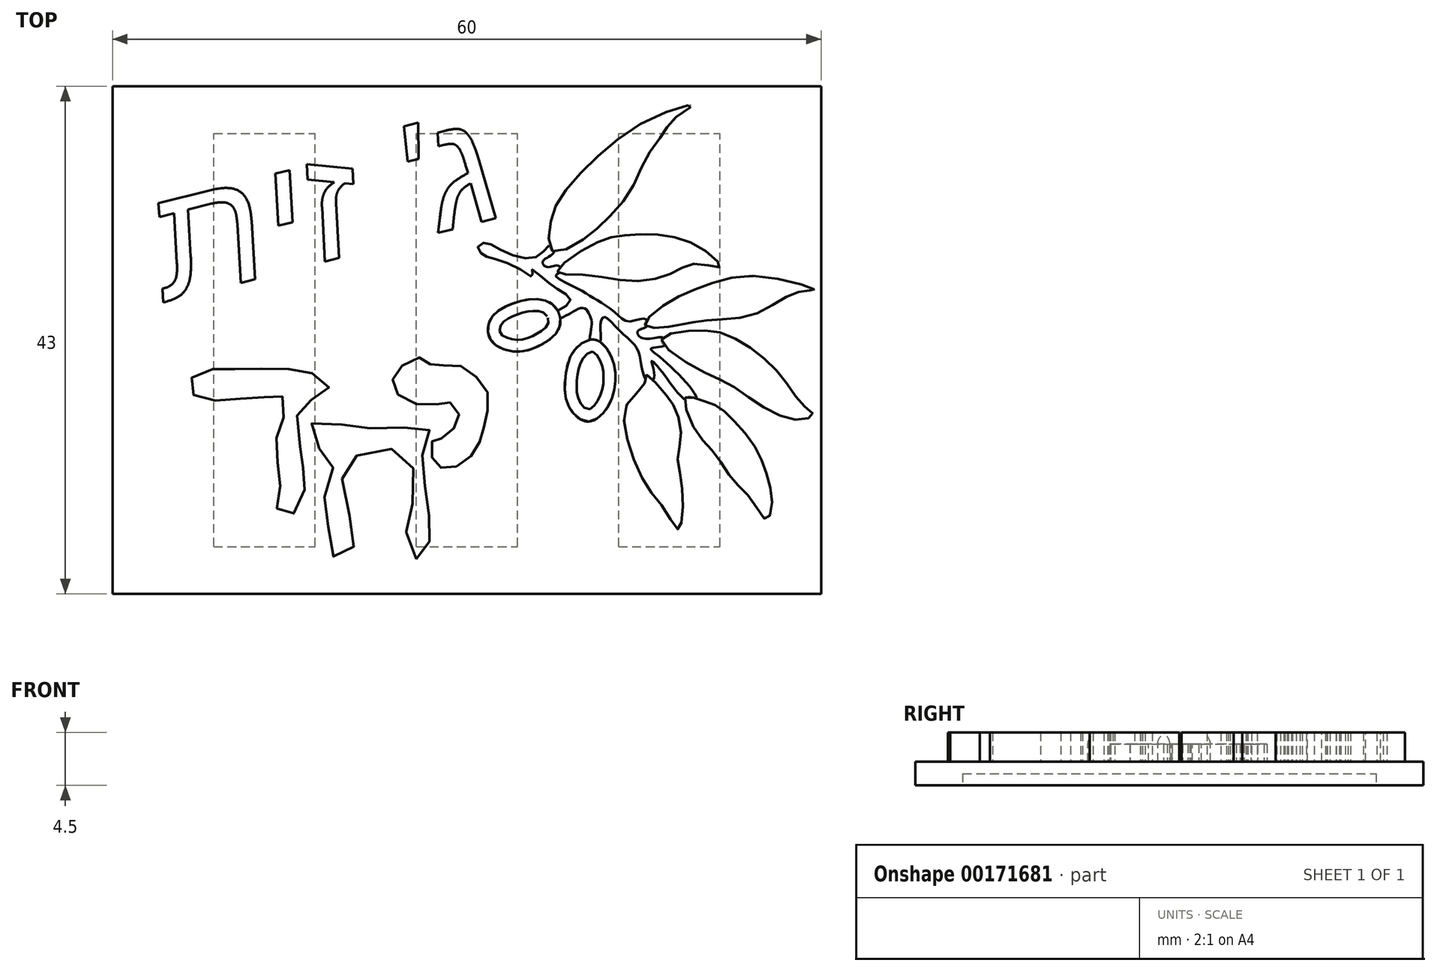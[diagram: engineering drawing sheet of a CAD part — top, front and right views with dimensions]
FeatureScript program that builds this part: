
annotation { "Feature Type Name" : "Feature", "Feature Type Description" : "" }
export const myFeature = defineFeature(function(context is Context, id is Id, definition is map)
    precondition{}
    {
        {
            var Q0;
            Q0=qCreatedBy(makeId("Top.planeOp"),FACE);
            var sketch = newSketch(context, id + "F0", { "sketchPlane" : qUnion([Q0])});
            skLineSegment(sketch, "E0.bottom", {"start": v(-30, 25) * mm, "end": v(30, 25) * mm});
            skLineSegment(sketch, "E0.top", {"start": v(-30, -18) * mm, "end": v(30, -18) * mm});
            skLineSegment(sketch, "E0.left", {"start": v(-30, 25) * mm, "end": v(-30, -18) * mm});
            skLineSegment(sketch, "E0.right", {"start": v(30, 25) * mm, "end": v(30, -18) * mm});
            skSolve(sketch);
        }
        {
            var Q0;
            Q0 = qSketchRegion(id + "F0", true);
            extrude(context, id + "F1", {"entities" : qUnion([Q0]), "depth" : 2 * mm});
        }
        {
            var Q0;
            Q0=makeQuery(id+"F1.opExtrude","CAP_FACE",FACE,{"disambiguationData":[OSD([sQuery(id+"F0.wireOp",EDGE,"E0.bottom"),sQuery(id+"F0.wireOp",EDGE,"E0.top"),sQuery(id+"F0.wireOp",EDGE,"E0.left"),sQuery(id+"F0.wireOp",EDGE,"E0.right")])],"isStart":false});
            var sketch = newSketch(context, id + "F2", { "sketchPlane" : qUnion([Q0])});
            skFitSpline(sketch, "E1", {"points": [v(-0.88, -7.22) * mm, v(0.62, -5.98) * mm, v(1.28, -4.61) * mm, v(1.6, -3.18) * mm, v(1.8, -1.09) * mm, v(0.52, 0.64) * mm, v(-1.27, 1.46) * mm, v(-2.83, 1.26) * mm, v(-3.62, 1.98) * mm, v(-5.31, 1.46) * mm, v(-6.3, 0) * mm, v(-5.48, -1.4) * mm, v(-2.83, -2) * mm, v(-1.6, -1.74) * mm, v(-0.68, -2.72) * mm, v(-1.07, -3.96) * mm, v(-2.25, -4.87) * mm, v(-2.83, -4.94) * mm, v(-2.98, -6.33) * mm, v(-2.3, -7.28) * mm, v(-0.88, -7.22) * mm]});
            skFitSpline(sketch, "E2", {"points": [v(-4.27, -15.05) * mm, v(-3.49, -14.46) * mm, v(-3.17, -13.55) * mm, v(-3.1, -12.56) * mm, v(-3.26, -10.9) * mm, v(-3.55, -9.18) * mm, v(-3.56, -7.69) * mm, v(-3.68, -5.66) * mm, v(-3.05, -4.32) * mm, v(-3.72, -3.93) * mm, v(-5.05, -3.9) * mm, v(-7.2, -4.02) * mm, v(-8.98, -3.93) * mm, v(-10.53, -3.7) * mm, v(-12.56, -3) * mm, v(-13.43, -4.94) * mm, v(-12.3, -5.79) * mm, v(-11.24, -6.81) * mm, v(-11.51, -7.68) * mm, v(-12.03, -9.57) * mm, v(-11.97, -11.4) * mm, v(-11.58, -12.9) * mm, v(-11.32, -14.73) * mm, v(-10.86, -15.25) * mm, v(-9.43, -13.68) * mm, v(-9.69, -12.05) * mm, v(-10.53, -9.24) * mm, v(-10.34, -7.42) * mm, v(-9.36, -6.33) * mm, v(-7.53, -5.92) * mm, v(-4.8, -5.98) * mm, v(-4.66, -8.79) * mm, v(-4.6, -10.48) * mm, v(-5.12, -12.05) * mm, v(-4.86, -13.94) * mm, v(-4.27, -15.05) * mm]});
            skFitSpline(sketch, "E3", {"points": [v(-16.1, -10.76) * mm, v(-15.1, -11.47) * mm, v(-13.94, -9.88) * mm, v(-13.71, -8.4) * mm, v(-13.96, -6.88) * mm, v(-14.12, -5.5) * mm, v(-14.32, -2.65) * mm, v(-13.43, -1.68) * mm, v(-11.84, -0.9) * mm, v(-11.84, 0) * mm, v(-13.71, 0.87) * mm, v(-15.23, 1.05) * mm, v(-17.58, 1.05) * mm, v(-19.67, 1.05) * mm, v(-21.14, 1.07) * mm, v(-22.68, 0.7) * mm, v(-23.61, -0.25) * mm, v(-23.03, -1.22) * mm, v(-21.5, -1.63) * mm, v(-19.67, -1.48) * mm, v(-17.65, -1.48) * mm, v(-16.54, -1.15) * mm, v(-15.56, -1.35) * mm, v(-15.36, -2.72) * mm, v(-16.08, -4.1) * mm, v(-16.02, -5.79) * mm, v(-16.02, -7.55) * mm, v(-15.82, -9.24) * mm, v(-16.1, -10.76) * mm]});
            skText(sketch, "E4", { "text": "תיז \'ג\n", "fontName": "Arimo-Italic.ttf"});
            skFitSpline(sketch, "E5", {"points": [v(7.82, 5.7) * mm, v(7, 6.7) * mm, v(5.22, 6.93) * mm, v(3.07, 6.23) * mm, v(1.96, 5.16) * mm, v(2.02, 3.5) * mm, v(4.18, 2.52) * mm, v(6.44, 3.18) * mm, v(7.78, 4.4) * mm, v(7.82, 5.7) * mm]});
            skFitSpline(sketch, "E6", {"points": [v(7.25, 11.03) * mm, v(9.49, 11.77) * mm, v(11.74, 13.6) * mm, v(13.93, 16.27) * mm, v(15.25, 19.05) * mm, v(16.68, 21.08) * mm, v(17.52, 22.26) * mm, v(19.1, 23.4) * mm, v(15.79, 22.36) * mm, v(10.63, 18.63) * mm, v(7.78, 15.3) * mm, v(7.02, 13) * mm, v(7.25, 11.03) * mm]});
            skFitSpline(sketch, "E7", {"points": [v(7.67, 9.3) * mm, v(9.76, 9.05) * mm, v(14.26, 8.5) * mm, v(17.63, 9.3) * mm, v(19.57, 9.98) * mm, v(21.46, 9.69) * mm, v(20.24, 11.03) * mm, v(16.72, 12.4) * mm, v(13.16, 12.35) * mm, v(10.53, 11.54) * mm, v(7.67, 9.3) * mm]});
            skFitSpline(sketch, "E8", {"points": [v(11, 3.48) * mm, v(9.93, 3.33) * mm, v(8.93, 2.37) * mm, v(8.37, 0.59) * mm, v(8.63, -2.12) * mm, v(10.24, -3.4) * mm, v(11.75, -2.45) * mm, v(12.53, -0.45) * mm, v(12.27, 2.03) * mm, v(11, 3.48) * mm]});
            skFitSpline(sketch, "E9", {"points": [v(15.08, 4.75) * mm, v(16.46, 6.3) * mm, v(20.02, 8.07) * mm, v(25.06, 8.88) * mm, v(29.43, 7.75) * mm, v(28.98, 7.7) * mm, v(27.34, 7.32) * mm, v(24.42, 5.7) * mm, v(20.8, 5.2) * mm, v(18.58, 4.9) * mm, v(16.68, 4.57) * mm, v(15.08, 4.75) * mm]});
            skFitSpline(sketch, "E10", {"points": [v(16.48, 3.55) * mm, v(18.7, 4.26) * mm, v(21.61, 4.08) * mm, v(24.65, 2.37) * mm, v(26.98, 0) * mm, v(28.56, -2.1) * mm, v(29.31, -2.8) * mm, v(28.44, -3.25) * mm, v(25.6, -2.48) * mm, v(22.46, -0.4) * mm, v(19.33, 1.17) * mm, v(16.48, 3.55) * mm]});
            skFitSpline(sketch, "E11", {"points": [v(15.23, 0.55) * mm, v(15.05, -0.24) * mm, v(13.62, -1.83) * mm, v(13.58, -4.9) * mm, v(15.2, -8.8) * mm, v(16.87, -11.04) * mm, v(17.91, -12.54) * mm, v(18.24, -11.57) * mm, v(18.14, -8.33) * mm, v(17.87, -6.37) * mm, v(18.16, -4.46) * mm, v(17.57, -2.18) * mm, v(16.74, -0.99) * mm, v(15.23, 0.55) * mm]});
            skFitSpline(sketch, "E12", {"points": [v(18.5, -1.38) * mm, v(19.36, -4.13) * mm, v(21, -6.14) * mm, v(22.52, -8.35) * mm, v(24.14, -10.07) * mm, v(25.37, -11.7) * mm, v(25.85, -10.44) * mm, v(25.4, -7.91) * mm, v(24.4, -5.54) * mm, v(22.36, -3.07) * mm, v(20.97, -1.99) * mm, v(19.48, -1.48) * mm, v(18.5, -1.38) * mm]});
            const initialGuessF2  = {"E4": [-0.02543, 0.00676, 0.96943, 0.24538, 0.00991]};
            skSetInitialGuess(sketch, initialGuessF2);
            skSolve(sketch);
        }
        {
            var Q0;
            Q0 = qSketchRegion(id + "F2", true);
            extrude(context, id + "F3", {"entities" : qUnion([Q0]), "operationType" : NewBodyOperationType.ADD, "depth" : 2.5 * mm});
        }
        {
            var Q0;
            Q0=makeQuery(id+"F2.imprint","IMPRINT",FACE,{"disambiguationData":[TD([[makeQuery(id+"F2.imprint","IMPRINT",EDGE,{"derivedFrom":sQuery(id+"F2.wireOp",EDGE,"E1")}),-1.0]])]});
            var sketch = newSketch(context, id + "F4", { "sketchPlane" : qUnion([Q0])});
            skFitSpline(sketch, "E13", {"points": [v(1.53, 11.76) * mm, v(0.94, 11.35) * mm, v(1.34, 10.75) * mm, v(2.04, 10.47) * mm, v(4.43, 9.57) * mm, v(5.6, 8.88) * mm, v(5.47, 9.45) * mm, v(6.53, 8.69) * mm, v(7.78, 7.77) * mm, v(8.77, 7.02) * mm, v(8.4, 6.4) * mm, v(7.34, 5.68) * mm, v(7.37, 5.24) * mm, v(8.27, 5.5) * mm, v(9.2, 6.02) * mm, v(9.91, 6.21) * mm, v(10.32, 5.8) * mm, v(10.56, 5.15) * mm, v(10.52, 4.34) * mm, v(10.52, 3.1) * mm, v(11.24, 3.15) * mm, v(11.3, 4.46) * mm, v(11.6, 5.45) * mm, v(12.83, 4.4) * mm, v(14.34, 2.9) * mm, v(14.78, 1.41) * mm, v(15.32, 0) * mm, v(15.87, 0.33) * mm, v(15.66, 1.7) * mm, v(16.9, 0.3) * mm, v(18.87, -1.77) * mm, v(19.47, -1.55) * mm, v(16.35, 2.05) * mm, v(15.62, 2.8) * mm, v(16.92, 3.13) * mm, v(16.79, 3.68) * mm, v(14.96, 3.64) * mm, v(14.47, 4.24) * mm, v(15.32, 4.71) * mm, v(15.13, 5.29) * mm, v(13.69, 5.08) * mm, v(12.4, 5.97) * mm, v(10.78, 7.02) * mm, v(9.37, 7.86) * mm, v(7.54, 8.97) * mm, v(7.97, 9.31) * mm, v(7.77, 9.8) * mm, v(6.79, 9.7) * mm, v(6.45, 10.18) * mm, v(7.4, 10.98) * mm, v(7.09, 11.54) * mm, v(6.4, 10.89) * mm, v(5.06, 10.42) * mm, v(2.6, 11.3) * mm, v(1.53, 11.76) * mm]});
            skSolve(sketch);
        }
        {
            var Q0;
            Q0 = qSketchRegion(id + "F4", true);
            extrude(context, id + "F5", {"entities" : qUnion([Q0]), "operationType" : NewBodyOperationType.ADD, "depth" : 1.5 * mm});
        }
        {
            var Q0;
            Q0=makeQuery(id+"F3.opExtrude","CAP_EDGE",EDGE,{"disambiguationData":[OSD([sQuery(id+"F2.wireOp",EDGE,"E5")])],"isStart":false});
            var Q1;
            Q1=makeQuery(id+"F3.opExtrude","CAP_EDGE",EDGE,{"disambiguationData":[OSD([sQuery(id+"F2.wireOp",EDGE,"E8")])],"isStart":false});
            fillet(context, id + "F6", {"entities" : qUnion([Q0, Q1]), "radius" : 1 * mm, "tangentPropagation" : true, "allowEdgeOverflow" : false});
        }
        {
            var Q0;
            Q0=makeQuery(id+"F1.opExtrude","CAP_FACE",FACE,{"disambiguationData":[OSD([sQuery(id+"F0.wireOp",EDGE,"E0.bottom"),sQuery(id+"F0.wireOp",EDGE,"E0.top"),sQuery(id+"F0.wireOp",EDGE,"E0.left"),sQuery(id+"F0.wireOp",EDGE,"E0.right")])],"isStart":true});
            var sketch = newSketch(context, id + "F7", { "sketchPlane" : qUnion([Q0])});
            skLineSegment(sketch, "E14.bottom", {"start": v(-21.43, 14) * mm, "end": v(-12.86, 14) * mm});
            skLineSegment(sketch, "E14.top", {"start": v(-21.43, -21) * mm, "end": v(-12.86, -21) * mm});
            skLineSegment(sketch, "E14.left", {"start": v(-21.43, 14) * mm, "end": v(-21.43, -21) * mm});
            skLineSegment(sketch, "E14.right", {"start": v(-12.86, 14) * mm, "end": v(-12.86, -21) * mm});
            skLineSegment(sketch, "E15.bottom", {"start": v(-4.29, 14) * mm, "end": v(4.29, 14) * mm});
            skLineSegment(sketch, "E15.top", {"start": v(-4.29, -21) * mm, "end": v(4.29, -21) * mm});
            skLineSegment(sketch, "E15.left", {"start": v(-4.29, 14) * mm, "end": v(-4.29, -21) * mm});
            skLineSegment(sketch, "E15.right", {"start": v(4.29, 14) * mm, "end": v(4.29, -21) * mm});
            skLineSegment(sketch, "E16.bottom", {"start": v(12.86, 14) * mm, "end": v(21.43, 14) * mm});
            skLineSegment(sketch, "E16.top", {"start": v(12.86, -21) * mm, "end": v(21.43, -21) * mm});
            skLineSegment(sketch, "E16.left", {"start": v(12.86, 14) * mm, "end": v(12.86, -21) * mm});
            skLineSegment(sketch, "E16.right", {"start": v(21.43, 14) * mm, "end": v(21.43, -21) * mm});
            skLineSegment(sketch, "E17", {"start": v(-21.43, -21) * mm, "end": v(-30, -21) * mm, "construction": true});
            skLineSegment(sketch, "E18", {"start": v(-4.29, -21) * mm, "end": v(-12.86, -21) * mm, "construction": true});
            skLineSegment(sketch, "E19", {"start": v(4.29, -21) * mm, "end": v(12.86, -21) * mm, "construction": true});
            skLineSegment(sketch, "E20", {"start": v(21.43, -21) * mm, "end": v(30, -21) * mm, "construction": true});
            skLineSegment(sketch, "E21", {"start": v(30, -21) * mm, "end": v(30, -25) * mm, "construction": true});
            skLineSegment(sketch, "E22", {"start": v(-21.43, 14) * mm, "end": v(-21.43, 18) * mm, "construction": true});
            skSolve(sketch);
        }
        {
            var Q0;
            Q0 = qSketchRegion(id + "F7", true);
            extrude(context, id + "F8", {"entities" : qUnion([Q0]), "operationType" : NewBodyOperationType.REMOVE, "oppositeDirection" : true, "depth" : 1 * mm});
        }
    });
